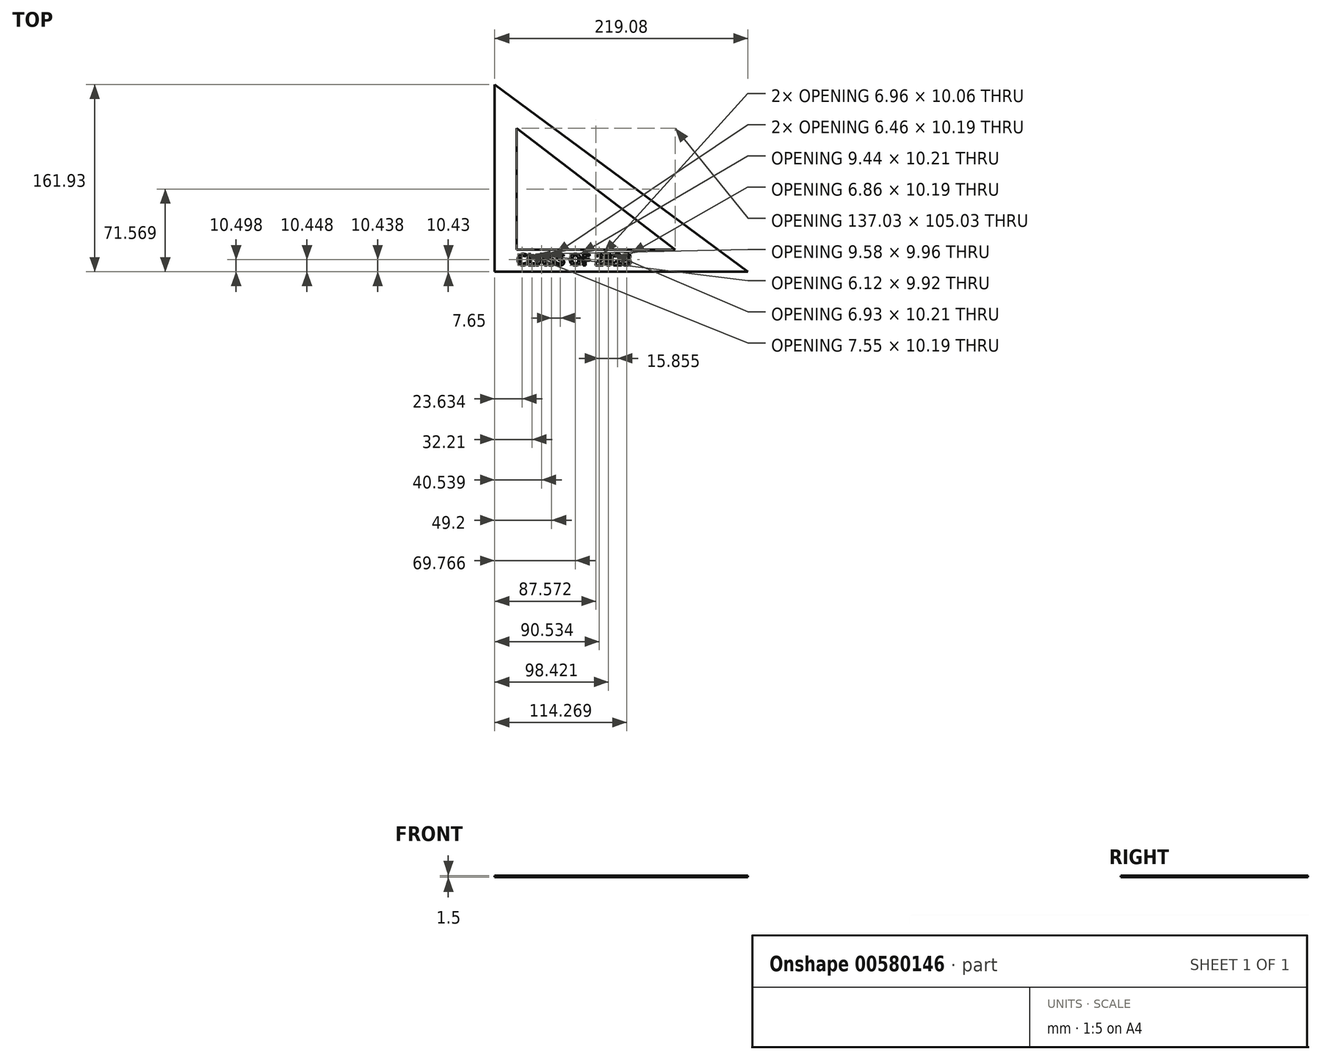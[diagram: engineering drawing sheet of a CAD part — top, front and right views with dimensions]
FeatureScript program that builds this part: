
annotation { "Feature Type Name" : "Feature", "Feature Type Description" : "" }
export const myFeature = defineFeature(function(context is Context, id is Id, definition is map)
    precondition{}
    {
        {
            var Q0;
            Q0=qCreatedBy(makeId("Top.planeOp"),FACE);
            var sketch = newSketch(context, id + "F0", { "sketchPlane" : qUnion([Q0])});
            skLineSegment(sketch, "E0", {"start": v(-110.4, -106.4) * mm, "end": v(-110.4, 109.5) * mm});
            skLineSegment(sketch, "E1", {"start": v(-110.4, 109.5) * mm, "end": v(181.7, -106.4) * mm});
            skLineSegment(sketch, "E2", {"start": v(181.7, -106.4) * mm, "end": v(-110.4, -106.4) * mm});
            skLineSegment(sketch, "E3", {"start": v(-85, 59.05) * mm, "end": v(-85, -81) * mm});
            skLineSegment(sketch, "E4", {"start": v(-85, -81) * mm, "end": v(97.72, -81) * mm});
            skLineSegment(sketch, "E5", {"start": v(97.72, -81) * mm, "end": v(-85, 59.05) * mm});
            skSolve(sketch);
        }
        {
            var Q0;
            Q0=makeQuery(id+"F0.imprint","IMPRINT",FACE,{"disambiguationData":[TD([[makeQuery(id+"F0.imprint","IMPRINT",EDGE,{"derivedFrom":sQuery(id+"F0.wireOp",EDGE,"E0")}),-1.0]])]});
            extrude(context, id + "F1", {"entities" : qUnion([Q0]), "depth" : 2 * mm, "offsetDistance" : 25.4 * mm});
        }
        {
            var Q0;
            Q0=makeQuery(id+"F1.opExtrude","SWEPT_BODY",BODY,{"disambiguationData":[OSD([sQuery(id+"F0.wireOp",EDGE,"E0"),sQuery(id+"F0.wireOp",EDGE,"E1"),sQuery(id+"F0.wireOp",EDGE,"E2"),sQuery(id+"F0.wireOp",EDGE,"E3"),sQuery(id+"F0.wireOp",EDGE,"E4"),sQuery(id+"F0.wireOp",EDGE,"E5")])]});
            var Q1;
            Q1=qCreatedBy(makeId("Origin.pointOp"),VERTEX);
            transform(context, id + "F2", {"entities" : qUnion([Q0]), "transformType" : TransformType.SCALE_UNIFORMLY, "scale" : 0.75, "scalePoint" : qUnion([Q1]), "makeCopy" : false});
        }
        {
            var Q0;
            Q0=makeQuery(id+"F1.opExtrude","CAP_FACE",FACE,{"disambiguationData":[OSD([sQuery(id+"F0.wireOp",EDGE,"E0"),sQuery(id+"F0.wireOp",EDGE,"E1"),sQuery(id+"F0.wireOp",EDGE,"E2"),sQuery(id+"F0.wireOp",EDGE,"E3"),sQuery(id+"F0.wireOp",EDGE,"E4"),sQuery(id+"F0.wireOp",EDGE,"E5")])],"isStart":false});
            var sketch = newSketch(context, id + "F3", { "sketchPlane" : qUnion([Q0])});
            skText(sketch, "E6", { "text": "CLASS OF 2023", "fontName": "OpenSans-Bold.ttf"});
            const initialGuessF3  = {"E6": [-0.06375, -0.07433, 1, 0, 0.01]};
            skSetInitialGuess(sketch, initialGuessF3);
            skSolve(sketch);
        }
        {
            var Q0;
            Q0=qSketchRegion(id+"F3",true);
            extrude(context, id + "F4", {"entities" : qUnion([Q0]), "operationType" : NewBodyOperationType.REMOVE, "endBound" : BoundingType.THROUGH_ALL, "oppositeDirection" : true, "depth" : 0.64 * mm, "offsetDistance" : 25.4 * mm});
        }
    });
